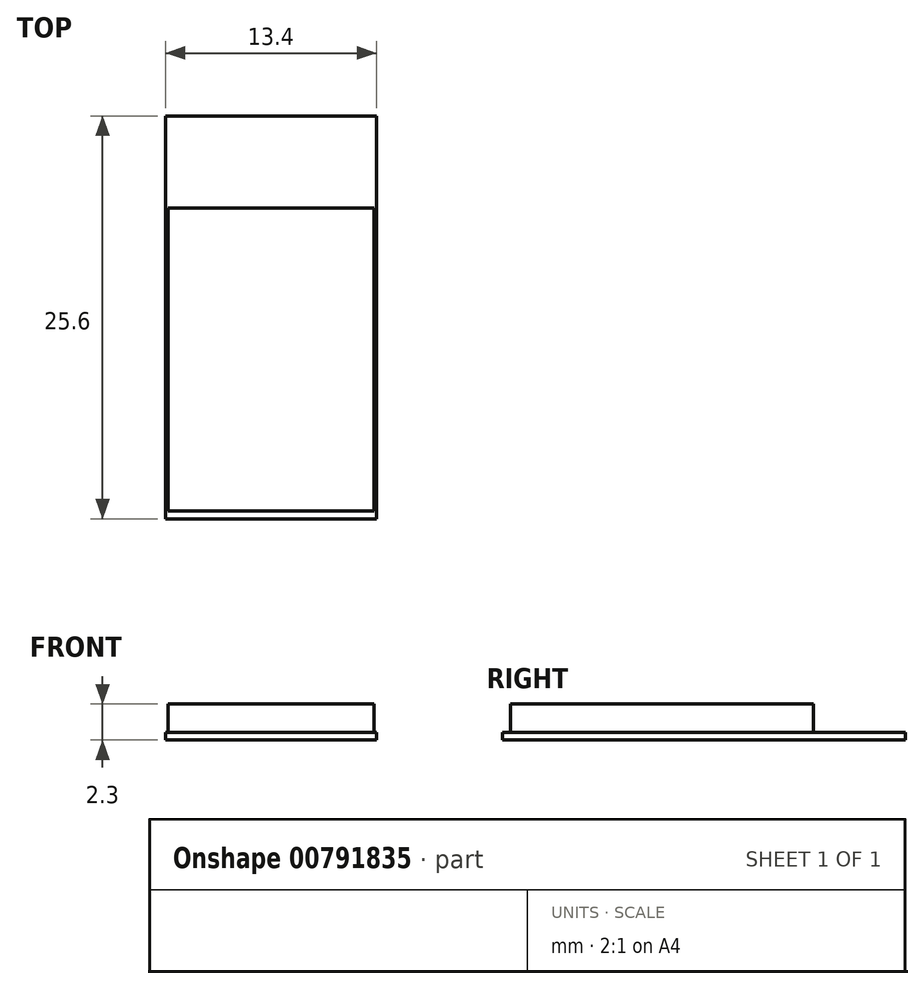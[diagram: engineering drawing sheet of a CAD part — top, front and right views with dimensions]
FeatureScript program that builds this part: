
annotation { "Feature Type Name" : "Feature", "Feature Type Description" : "" }
export const myFeature = defineFeature(function(context is Context, id is Id, definition is map)
    precondition{}
    {
        {
            var Q0;
            Q0=qCreatedBy(makeId("Top.planeOp"),FACE);
            var sketch = newSketch(context, id + "F0", { "sketchPlane" : qUnion([Q0])});
            skLineSegment(sketch, "E0.bottom", {"start": v(0, 0) * mm, "end": v(13.4, 0) * mm});
            skLineSegment(sketch, "E0.top", {"start": v(0, 25.6) * mm, "end": v(13.4, 25.6) * mm});
            skLineSegment(sketch, "E0.left", {"start": v(0, 0) * mm, "end": v(0, 25.6) * mm});
            skLineSegment(sketch, "E0.right", {"start": v(13.4, 0) * mm, "end": v(13.4, 25.6) * mm});
            skSolve(sketch);
        }
        {
            var Q0;
            Q0=makeQuery(id+"F0.imprint","IMPRINT",FACE,{"disambiguationData":[TD([[makeQuery(id+"F0.imprint","IMPRINT",EDGE,{"derivedFrom":sQuery(id+"F0.wireOp",EDGE,"E0.bottom")}),1.0]])]});
            extrude(context, id + "F1", {"entities" : qUnion([Q0]), "depth" : .5 * mm, "offsetDistance" : 25 * mm});
        }
        {
            var Q0;
            Q0=makeQuery(id+"F1.opExtrude","CAP_FACE",FACE,{"disambiguationData":[OSD([sQuery(id+"F0.wireOp",EDGE,"E0.bottom"),sQuery(id+"F0.wireOp",EDGE,"E0.top"),sQuery(id+"F0.wireOp",EDGE,"E0.left"),sQuery(id+"F0.wireOp",EDGE,"E0.right")])],"isStart":false});
            var sketch = newSketch(context, id + "F2", { "sketchPlane" : qUnion([Q0])});
            skLineSegment(sketch, "E1.bottom", {"start": v(0.15, 0.5) * mm, "end": v(13.25, 0.5) * mm});
            skLineSegment(sketch, "E1.top", {"start": v(0.15, 19.75) * mm, "end": v(13.25, 19.75) * mm});
            skLineSegment(sketch, "E1.left", {"start": v(0.15, 0.5) * mm, "end": v(0.15, 19.75) * mm});
            skLineSegment(sketch, "E1.right", {"start": v(13.25, 0.5) * mm, "end": v(13.25, 19.75) * mm});
            skSolve(sketch);
        }
        {
            var Q0;
            Q0 = qSketchRegion(id + "F2", true);
            extrude(context, id + "F3", {"entities" : qUnion([Q0]), "operationType" : NewBodyOperationType.ADD, "depth" : (2.3 - .5) * mm, "offsetDistance" : 25 * mm});
        }
    });
